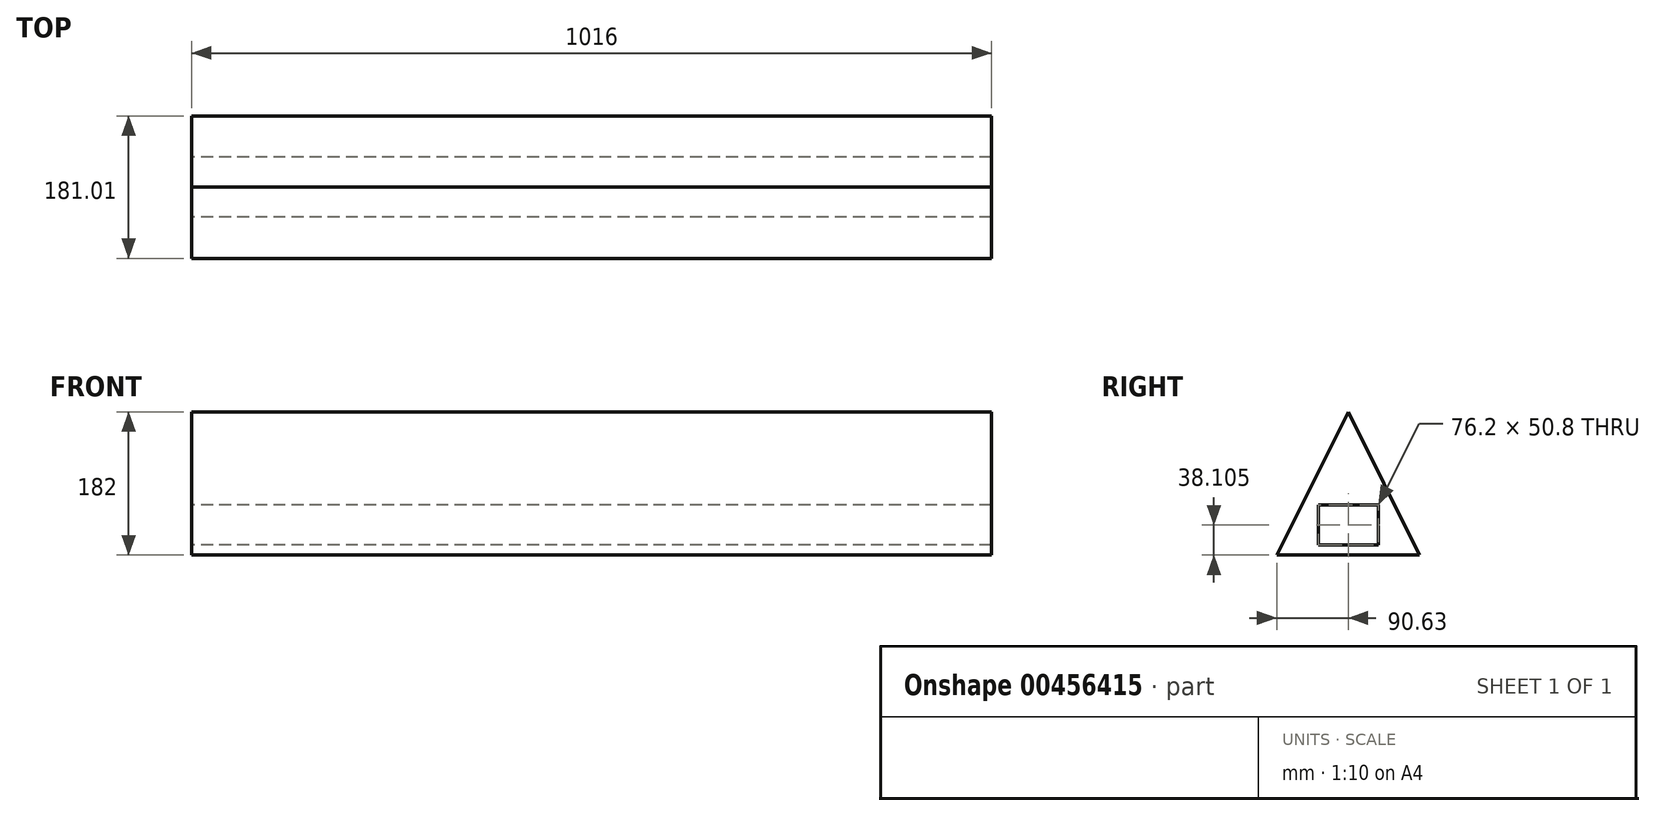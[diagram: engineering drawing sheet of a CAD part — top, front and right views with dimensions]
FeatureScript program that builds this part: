
annotation { "Feature Type Name" : "Feature", "Feature Type Description" : "" }
export const myFeature = defineFeature(function(context is Context, id is Id, definition is map)
    precondition{}
    {
        {
            var Q0;
            Q0=qCreatedBy(makeId("Right.planeOp"),FACE);
            var sketch = newSketch(context, id + "F0", { "sketchPlane" : qUnion([Q0])});
            skLineSegment(sketch, "E0", {"start": v(-90.63, -90.63) * mm, "end": v(90.38, -90.63) * mm});
            skLineSegment(sketch, "E1", {"start": v(90.38, -90.63) * mm, "end": v(0, 91.37) * mm});
            skLineSegment(sketch, "E2", {"start": v(0, 91.37) * mm, "end": v(-90.63, -90.63) * mm});
            skLineSegment(sketch, "E3.bottom", {"start": v(-38.1, -27.13) * mm, "end": v(38.1, -27.13) * mm});
            skLineSegment(sketch, "E3.top", {"start": v(-38.1, -77.93) * mm, "end": v(38.1, -77.93) * mm});
            skLineSegment(sketch, "E3.left", {"start": v(-38.1, -27.13) * mm, "end": v(-38.1, -77.93) * mm});
            skLineSegment(sketch, "E3.right", {"start": v(38.1, -27.13) * mm, "end": v(38.1, -77.93) * mm});
            skPoint(sketch, "E3.middle", {"position": v(0, -52.53) * mm});
            skSolve(sketch);
        }
        {
            var Q0;
            Q0=makeQuery(id+"F0.imprint","IMPRINT",FACE,{"disambiguationData":[TD([[makeQuery(id+"F0.imprint","IMPRINT",EDGE,{"derivedFrom":sQuery(id+"F0.wireOp",EDGE,"E0")}),1.0]])]});
            extrude(context, id + "F1", {"entities" : qUnion([Q0]), "depth" : 1016 * mm});
        }
    });
